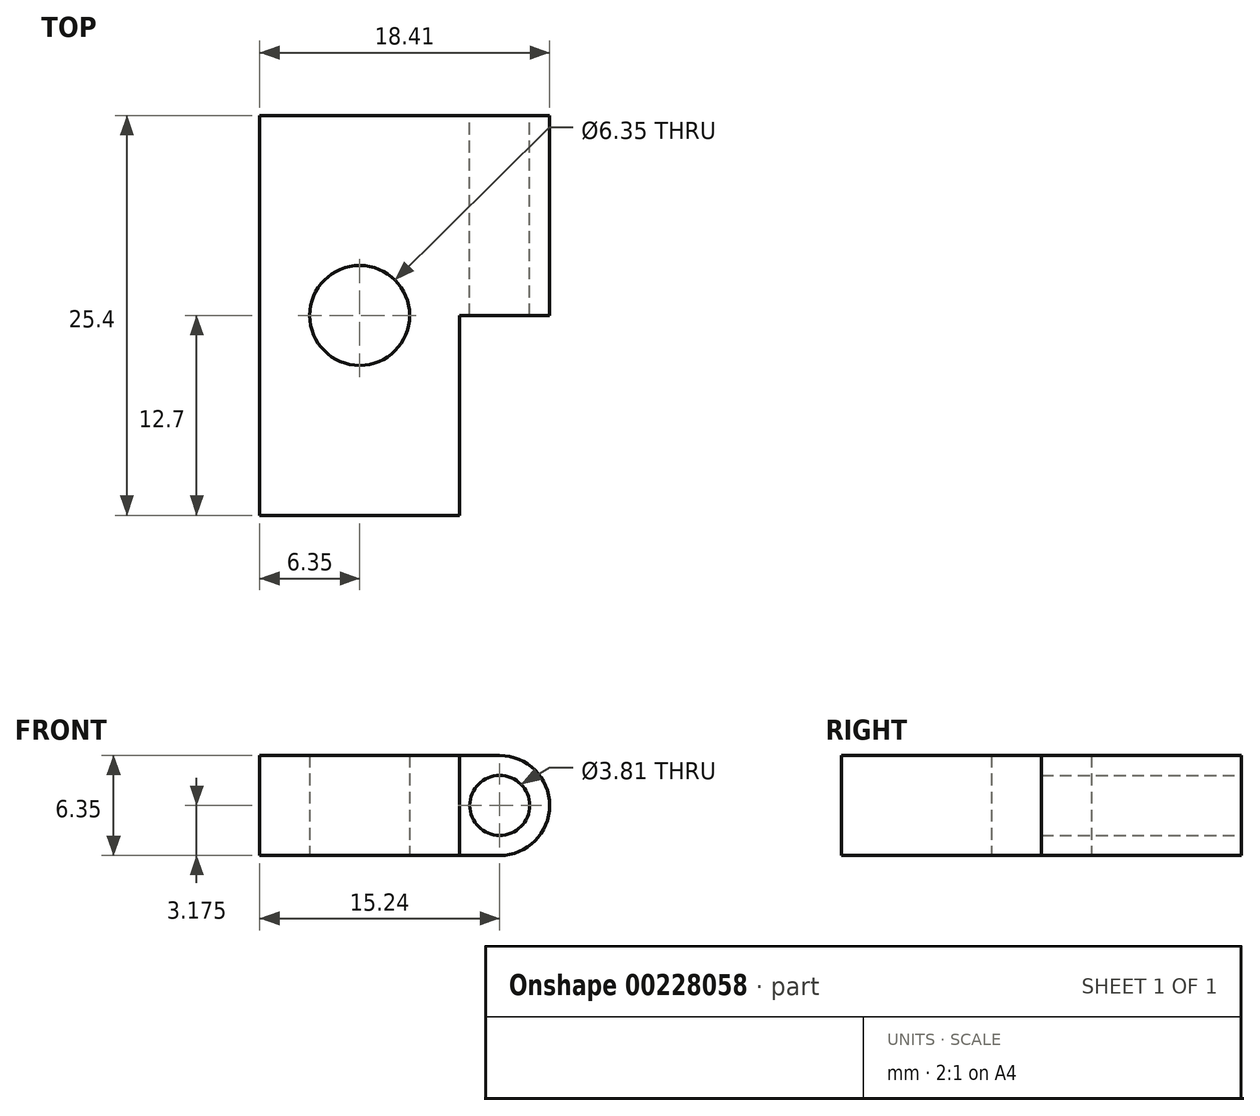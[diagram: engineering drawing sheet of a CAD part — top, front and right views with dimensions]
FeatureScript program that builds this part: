
annotation { "Feature Type Name" : "Feature", "Feature Type Description" : "" }
export const myFeature = defineFeature(function(context is Context, id is Id, definition is map)
    precondition{}
    {
        {
            var Q0;
            Q0=qCreatedBy(makeId("Top.planeOp"),FACE);
            var sketch = newSketch(context, id + "F0", { "sketchPlane" : qUnion([Q0])});
            skLineSegment(sketch, "E0.bottom", {"start": v(0, 0) * mm, "end": v(12.7, 0) * mm});
            skLineSegment(sketch, "E0.top", {"start": v(0, 25.4) * mm, "end": v(12.7, 25.4) * mm});
            skLineSegment(sketch, "E0.left", {"start": v(0, 0) * mm, "end": v(0, 25.4) * mm});
            skLineSegment(sketch, "E0.right", {"start": v(12.7, 0) * mm, "end": v(12.7, 25.4) * mm});
            skCircle(sketch, "E1", {"center": v(6.35, 12.7) * mm, "radius": 3.18 * mm});
            skLineSegment(sketch, "E2", {"start": v(0, 12.7) * mm, "end": v(12.7, 12.7) * mm, "construction": true});
            skSolve(sketch);
        }
        {
            var Q0;
            Q0 = qSketchRegion(id + "F0", true);
            extrude(context, id + "F1", {"entities" : qUnion([Q0]), "depth" : 6.35 * mm, "offsetDistance" : 25.4 * mm});
        }
        {
            var Q0;
            Q0=makeQuery(id+"F1.opExtrude","SWEPT_FACE",FACE,{"disambiguationData":[OSD([sQuery(id+"F0.wireOp",EDGE,"E0.top")])]});
            var sketch = newSketch(context, id + "F2", { "sketchPlane" : qUnion([Q0])});
            skLineSegment(sketch, "E3", {"start": v(-12.7, 6.35) * mm, "end": v(-12.7, 0) * mm});
            skLineSegment(sketch, "E4", {"start": v(-12.7, 0) * mm, "end": v(-15.24, 0) * mm});
            skLineSegment(sketch, "E5", {"start": v(-12.7, 6.35) * mm, "end": v(-15.24, 6.35) * mm});
            skArc(sketch, "E6", {"start": v(-15.24, 6.35) * mm, "mid": v(-18.41, 3.18) * mm, "end": v(-15.24, 0) * mm});
            skCircle(sketch, "E7", {"center": v(-15.24, 3.18) * mm, "radius": 1.9 * mm});
            skSolve(sketch);
        }
        {
            var Q0;
            Q0 = qSketchRegion(id + "F2", true);
            extrude(context, id + "F3", {"entities" : qUnion([Q0]), "operationType" : NewBodyOperationType.ADD, "oppositeDirection" : true, "depth" : 12.7 * mm, "offsetDistance" : 25.4 * mm});
        }
    });
